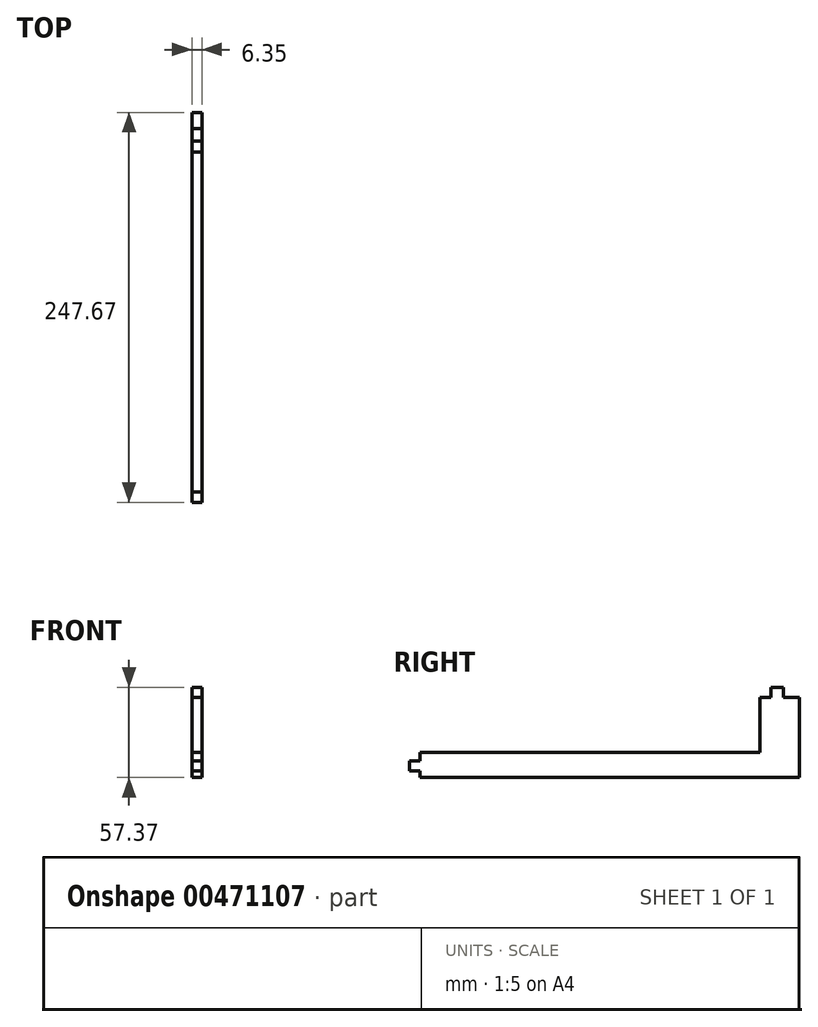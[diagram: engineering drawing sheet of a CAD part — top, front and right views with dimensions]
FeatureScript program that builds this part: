
annotation { "Feature Type Name" : "Feature", "Feature Type Description" : "" }
export const myFeature = defineFeature(function(context is Context, id is Id, definition is map)
    precondition{}
    {
        {
            var Q0;
            Q0=qCreatedBy(makeId("Right.planeOp"),FACE);
            var sketch = newSketch(context, id + "F0", { "sketchPlane" : qUnion([Q0])});
            skLineSegment(sketch, "E0", {"start": v(0, 0) * mm, "end": v(-6.6, 0) * mm});
            skLineSegment(sketch, "E1", {"start": v(-6.6, 0) * mm, "end": v(-6.6, -6.35) * mm});
            skLineSegment(sketch, "E2", {"start": v(-6.6, -6.35) * mm, "end": v(0, -6.35) * mm});
            skLineSegment(sketch, "E3", {"start": v(0, -6.35) * mm, "end": v(0, -10.46) * mm});
            skLineSegment(sketch, "E4", {"start": v(0, 0) * mm, "end": v(0, 5.38) * mm});
            skLineSegment(sketch, "E5", {"start": v(0, 5.38) * mm, "end": v(215.9, 5.38) * mm});
            skLineSegment(sketch, "E6", {"start": v(215.9, 5.38) * mm, "end": v(215.9, 40.3) * mm});
            skLineSegment(sketch, "E7", {"start": v(215.9, 40.3) * mm, "end": v(222.88, 40.3) * mm});
            skLineSegment(sketch, "E8", {"start": v(222.88, 40.3) * mm, "end": v(222.88, 46.91) * mm});
            skLineSegment(sketch, "E9", {"start": v(222.88, 46.91) * mm, "end": v(230.9, 46.91) * mm});
            skLineSegment(sketch, "E10", {"start": v(230.9, 46.91) * mm, "end": v(230.9, 40.3) * mm});
            skLineSegment(sketch, "E11", {"start": v(230.9, 40.3) * mm, "end": v(241.07, 40.3) * mm});
            skLineSegment(sketch, "E12", {"start": v(0, -10.46) * mm, "end": v(241.07, -10.46) * mm});
            skLineSegment(sketch, "E13", {"start": v(241.07, 40.3) * mm, "end": v(241.07, -10.46) * mm});
            skSolve(sketch);
        }
        {
            var Q0;
            Q0=makeQuery(id+"F0.imprint","IMPRINT",FACE,{"disambiguationData":[TD([[makeQuery(id+"F0.imprint","IMPRINT",EDGE,{"derivedFrom":sQuery(id+"F0.wireOp",EDGE,"E0")}),1.0]])]});
            extrude(context, id + "F1", {"entities" : qUnion([Q0]), "depth" : 6.35 * mm});
        }
    });
